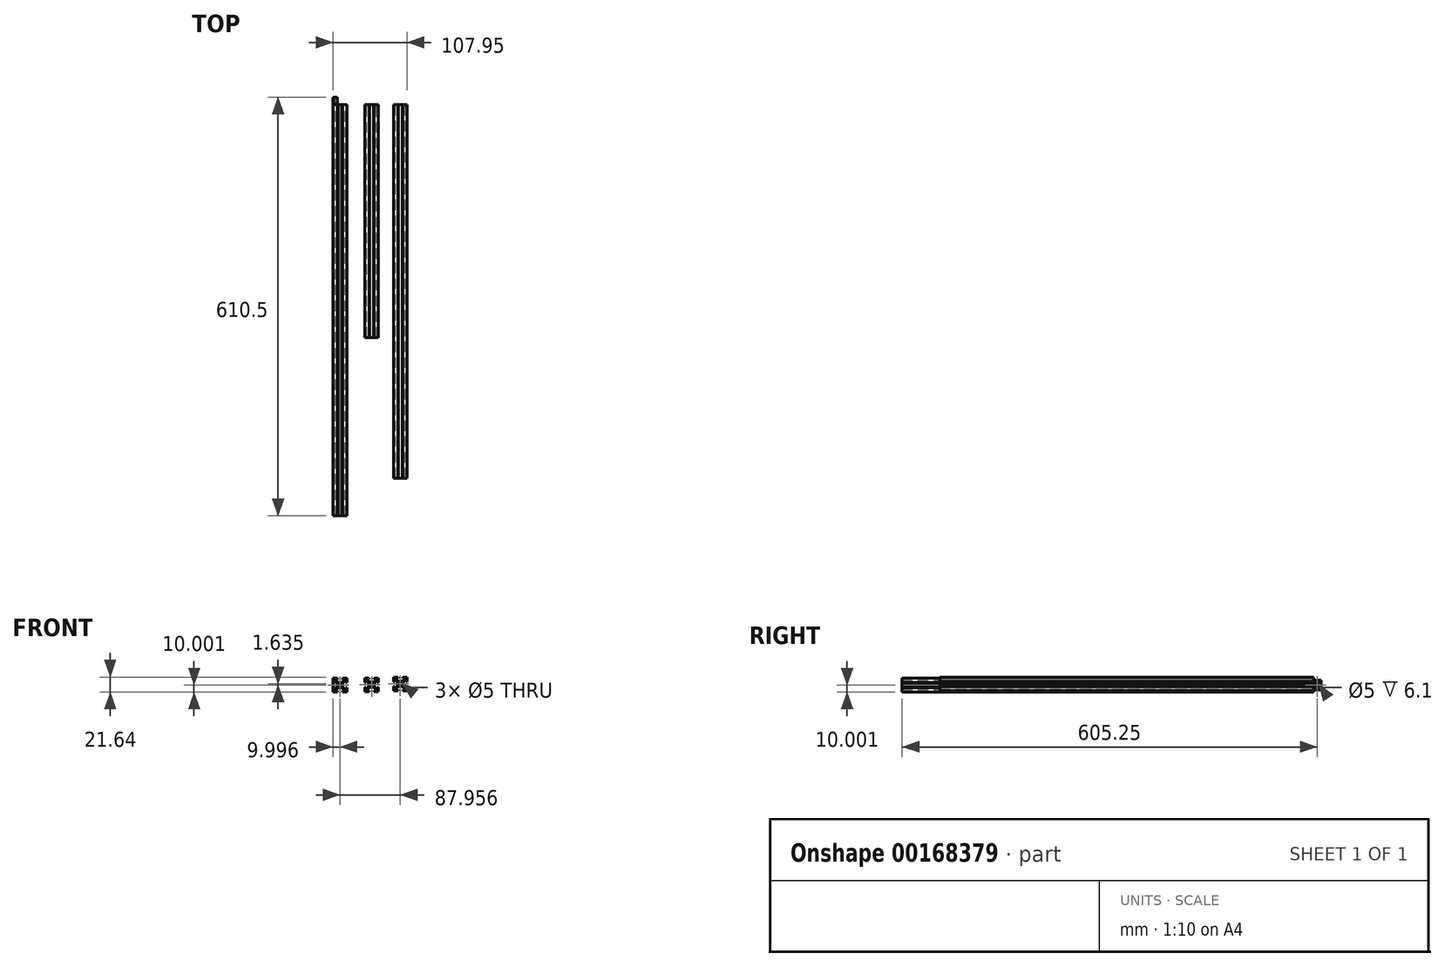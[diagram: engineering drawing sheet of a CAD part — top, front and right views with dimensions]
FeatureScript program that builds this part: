
annotation { "Feature Type Name" : "Feature", "Feature Type Description" : "" }
export const myFeature = defineFeature(function(context is Context, id is Id, definition is map)
    precondition{}
    {
        {
            var Q0;
            Q0=qCreatedBy(makeId("Front.planeOp"),FACE);
            var sketch = newSketch(context, id + "F0", { "sketchPlane" : qUnion([Q0])});
            skLineSegment(sketch, "E0", {"start": v(-6.67, 58.37) * mm, "end": v(-13.07, 58.37) * mm});
            skLineSegment(sketch, "E1", {"start": v(-13.07, 58.37) * mm, "end": v(-13.07, 51.97) * mm});
            skLineSegment(sketch, "E2", {"start": v(-13.07, 51.97) * mm, "end": v(-11.54, 51.97) * mm});
            skLineSegment(sketch, "E3", {"start": v(-11.54, 51.97) * mm, "end": v(-11.54, 55.42) * mm});
            skLineSegment(sketch, "E4", {"start": v(-11.54, 55.42) * mm, "end": v(-6.97, 50.81) * mm});
            skLineSegment(sketch, "E5", {"start": v(-6.97, 50.81) * mm, "end": v(-6.97, 45.93) * mm});
            skLineSegment(sketch, "E6", {"start": v(-6.97, 45.93) * mm, "end": v(-11.54, 41.32) * mm});
            skLineSegment(sketch, "E7", {"start": v(-11.54, 41.32) * mm, "end": v(-11.54, 44.77) * mm});
            skLineSegment(sketch, "E8", {"start": v(-11.54, 44.77) * mm, "end": v(-13.07, 44.77) * mm});
            skLineSegment(sketch, "E9", {"start": v(-13.07, 44.77) * mm, "end": v(-13.07, 38.37) * mm});
            skLineSegment(sketch, "E10", {"start": v(-13.07, 38.37) * mm, "end": v(-6.67, 38.37) * mm});
            skLineSegment(sketch, "E11", {"start": v(-6.67, 38.37) * mm, "end": v(-6.67, 39.9) * mm});
            skLineSegment(sketch, "E12", {"start": v(-6.67, 39.9) * mm, "end": v(-10.13, 39.9) * mm});
            skLineSegment(sketch, "E13", {"start": v(-10.13, 39.9) * mm, "end": v(-5.57, 44.5) * mm});
            skLineSegment(sketch, "E14", {"start": v(-5.57, 44.5) * mm, "end": v(-0.58, 44.5) * mm});
            skLineSegment(sketch, "E15", {"start": v(-0.58, 44.5) * mm, "end": v(3.98, 39.9) * mm});
            skLineSegment(sketch, "E16", {"start": v(3.98, 39.9) * mm, "end": v(0.53, 39.9) * mm});
            skLineSegment(sketch, "E17", {"start": v(0.53, 39.9) * mm, "end": v(0.53, 38.37) * mm});
            skLineSegment(sketch, "E18", {"start": v(0.53, 38.37) * mm, "end": v(6.93, 38.37) * mm});
            skLineSegment(sketch, "E19", {"start": v(6.93, 38.37) * mm, "end": v(6.93, 44.77) * mm});
            skLineSegment(sketch, "E20", {"start": v(6.93, 44.77) * mm, "end": v(5.4, 44.77) * mm});
            skLineSegment(sketch, "E21", {"start": v(5.4, 44.77) * mm, "end": v(5.4, 41.32) * mm});
            skLineSegment(sketch, "E22", {"start": v(5.4, 41.32) * mm, "end": v(0.83, 45.93) * mm});
            skLineSegment(sketch, "E23", {"start": v(0.83, 45.93) * mm, "end": v(0.83, 50.81) * mm});
            skLineSegment(sketch, "E24", {"start": v(0.83, 50.81) * mm, "end": v(5.4, 55.42) * mm});
            skLineSegment(sketch, "E25", {"start": v(5.4, 55.42) * mm, "end": v(5.4, 51.97) * mm});
            skLineSegment(sketch, "E26", {"start": v(5.4, 51.97) * mm, "end": v(6.93, 51.97) * mm});
            skLineSegment(sketch, "E27", {"start": v(6.93, 51.97) * mm, "end": v(6.93, 58.37) * mm});
            skLineSegment(sketch, "E28", {"start": v(6.93, 58.37) * mm, "end": v(0.53, 58.37) * mm});
            skLineSegment(sketch, "E29", {"start": v(0.53, 58.37) * mm, "end": v(0.53, 56.84) * mm});
            skLineSegment(sketch, "E30", {"start": v(0.53, 56.84) * mm, "end": v(3.98, 56.84) * mm});
            skLineSegment(sketch, "E31", {"start": v(3.98, 56.84) * mm, "end": v(-0.58, 52.24) * mm});
            skLineSegment(sketch, "E32", {"start": v(-0.58, 52.24) * mm, "end": v(-5.57, 52.24) * mm});
            skLineSegment(sketch, "E33", {"start": v(-5.57, 52.24) * mm, "end": v(-10.13, 56.84) * mm});
            skLineSegment(sketch, "E34", {"start": v(-10.13, 56.84) * mm, "end": v(-6.67, 56.84) * mm});
            skLineSegment(sketch, "E35", {"start": v(-6.67, 56.84) * mm, "end": v(-6.67, 58.37) * mm});
            skCircle(sketch, "E36", {"center": v(-3.07, 48.37) * mm, "radius": 2.5 * mm});
            skCircle(sketch, "E37", {"center": v(-3.07, 48.37) * mm, "radius": 4.6 * mm, "construction": true});
            skCircle(sketch, "E38", {"center": v(-3.07, 48.37) * mm, "radius": 9.2 * mm, "construction": true});
            skCircle(sketch, "E39", {"center": v(-3.07, 48.37) * mm, "radius": 14.14 * mm, "construction": true});
            skLineSegment(sketch, "E40", {"start": v(39.48, 58.74) * mm, "end": v(33.08, 58.74) * mm});
            skLineSegment(sketch, "E41", {"start": v(33.08, 58.74) * mm, "end": v(33.08, 52.34) * mm});
            skLineSegment(sketch, "E42", {"start": v(33.08, 52.34) * mm, "end": v(34.6, 52.34) * mm});
            skLineSegment(sketch, "E43", {"start": v(34.6, 52.34) * mm, "end": v(34.6, 55.8) * mm});
            skLineSegment(sketch, "E44", {"start": v(34.6, 55.8) * mm, "end": v(39.05, 50.97) * mm});
            skLineSegment(sketch, "E45", {"start": v(39.05, 50.97) * mm, "end": v(39.05, 46.52) * mm});
            skLineSegment(sketch, "E46", {"start": v(39.05, 46.52) * mm, "end": v(34.6, 41.68) * mm});
            skLineSegment(sketch, "E47", {"start": v(34.6, 41.68) * mm, "end": v(34.6, 45.14) * mm});
            skLineSegment(sketch, "E48", {"start": v(34.6, 45.14) * mm, "end": v(33.08, 45.14) * mm});
            skLineSegment(sketch, "E49", {"start": v(33.08, 45.14) * mm, "end": v(33.08, 38.74) * mm});
            skLineSegment(sketch, "E50", {"start": v(33.08, 38.74) * mm, "end": v(39.48, 38.74) * mm});
            skLineSegment(sketch, "E51", {"start": v(39.48, 38.74) * mm, "end": v(39.48, 40.27) * mm});
            skLineSegment(sketch, "E52", {"start": v(39.48, 40.27) * mm, "end": v(36.02, 40.27) * mm});
            skLineSegment(sketch, "E53", {"start": v(36.02, 40.27) * mm, "end": v(40.38, 45.01) * mm});
            skLineSegment(sketch, "E54", {"start": v(40.38, 45.01) * mm, "end": v(45.77, 45.01) * mm});
            skLineSegment(sketch, "E55", {"start": v(45.77, 45.01) * mm, "end": v(50.14, 40.27) * mm});
            skLineSegment(sketch, "E56", {"start": v(50.14, 40.27) * mm, "end": v(46.68, 40.27) * mm});
            skLineSegment(sketch, "E57", {"start": v(46.68, 40.27) * mm, "end": v(46.68, 38.74) * mm});
            skLineSegment(sketch, "E58", {"start": v(46.68, 38.74) * mm, "end": v(53.08, 38.74) * mm});
            skLineSegment(sketch, "E59", {"start": v(53.08, 38.74) * mm, "end": v(53.08, 45.14) * mm});
            skLineSegment(sketch, "E60", {"start": v(53.08, 45.14) * mm, "end": v(51.56, 45.14) * mm});
            skLineSegment(sketch, "E61", {"start": v(51.56, 45.14) * mm, "end": v(51.56, 41.68) * mm});
            skLineSegment(sketch, "E62", {"start": v(51.56, 41.68) * mm, "end": v(47.1, 46.52) * mm});
            skLineSegment(sketch, "E63", {"start": v(47.1, 46.52) * mm, "end": v(47.1, 50.97) * mm});
            skLineSegment(sketch, "E64", {"start": v(47.1, 50.97) * mm, "end": v(51.56, 55.8) * mm});
            skLineSegment(sketch, "E65", {"start": v(51.56, 55.8) * mm, "end": v(51.56, 52.34) * mm});
            skLineSegment(sketch, "E66", {"start": v(51.56, 52.34) * mm, "end": v(53.08, 52.34) * mm});
            skLineSegment(sketch, "E67", {"start": v(53.08, 52.34) * mm, "end": v(53.08, 58.74) * mm});
            skLineSegment(sketch, "E68", {"start": v(53.08, 58.74) * mm, "end": v(46.68, 58.74) * mm});
            skLineSegment(sketch, "E69", {"start": v(46.68, 58.74) * mm, "end": v(46.68, 57.22) * mm});
            skLineSegment(sketch, "E70", {"start": v(46.68, 57.22) * mm, "end": v(50.14, 57.22) * mm});
            skLineSegment(sketch, "E71", {"start": v(50.14, 57.22) * mm, "end": v(45.77, 52.48) * mm});
            skLineSegment(sketch, "E72", {"start": v(45.77, 52.48) * mm, "end": v(40.38, 52.48) * mm});
            skLineSegment(sketch, "E73", {"start": v(40.38, 52.48) * mm, "end": v(36.02, 57.22) * mm});
            skLineSegment(sketch, "E74", {"start": v(36.02, 57.22) * mm, "end": v(39.48, 57.22) * mm});
            skLineSegment(sketch, "E75", {"start": v(39.48, 57.22) * mm, "end": v(39.48, 58.74) * mm});
            skCircle(sketch, "E76", {"center": v(43.08, 48.74) * mm, "radius": 2.5 * mm});
            skCircle(sketch, "E77", {"center": v(43.08, 48.74) * mm, "radius": 4.6 * mm, "construction": true});
            skCircle(sketch, "E78", {"center": v(43.08, 48.74) * mm, "radius": 9.2 * mm, "construction": true});
            skCircle(sketch, "E79", {"center": v(43.08, 48.74) * mm, "radius": 14.14 * mm, "construction": true});
            skLineSegment(sketch, "E80.bottom", {"start": v(-13.07, 58.37) * mm, "end": v(6.93, 58.37) * mm, "construction": true});
            skLineSegment(sketch, "E80.top", {"start": v(-13.07, 38.37) * mm, "end": v(6.93, 38.37) * mm, "construction": true});
            skLineSegment(sketch, "E80.left", {"start": v(-13.07, 58.37) * mm, "end": v(-13.07, 38.37) * mm, "construction": true});
            skLineSegment(sketch, "E80.right", {"start": v(6.93, 58.37) * mm, "end": v(6.93, 38.37) * mm, "construction": true});
            skLineSegment(sketch, "E81", {"start": v(81.28, 60) * mm, "end": v(74.88, 60) * mm});
            skLineSegment(sketch, "E82", {"start": v(74.88, 60) * mm, "end": v(74.88, 53.6) * mm});
            skLineSegment(sketch, "E83", {"start": v(74.88, 53.6) * mm, "end": v(76.4, 53.6) * mm});
            skLineSegment(sketch, "E84", {"start": v(76.4, 53.6) * mm, "end": v(76.4, 57.07) * mm});
            skLineSegment(sketch, "E85", {"start": v(76.4, 57.07) * mm, "end": v(80.85, 52.22) * mm});
            skLineSegment(sketch, "E86", {"start": v(80.85, 52.22) * mm, "end": v(80.85, 47.79) * mm});
            skLineSegment(sketch, "E87", {"start": v(80.85, 47.79) * mm, "end": v(76.4, 42.94) * mm});
            skLineSegment(sketch, "E88", {"start": v(76.4, 42.94) * mm, "end": v(76.4, 46.4) * mm});
            skLineSegment(sketch, "E89", {"start": v(76.4, 46.4) * mm, "end": v(74.88, 46.4) * mm});
            skLineSegment(sketch, "E90", {"start": v(74.88, 46.4) * mm, "end": v(74.88, 40) * mm});
            skLineSegment(sketch, "E91", {"start": v(74.88, 40) * mm, "end": v(81.28, 40) * mm});
            skLineSegment(sketch, "E92", {"start": v(81.28, 40) * mm, "end": v(81.28, 41.53) * mm});
            skLineSegment(sketch, "E93", {"start": v(81.28, 41.53) * mm, "end": v(77.82, 41.53) * mm});
            skLineSegment(sketch, "E94", {"start": v(77.82, 41.53) * mm, "end": v(82.18, 46.28) * mm});
            skLineSegment(sketch, "E95", {"start": v(82.18, 46.28) * mm, "end": v(87.59, 46.28) * mm});
            skLineSegment(sketch, "E96", {"start": v(87.59, 46.28) * mm, "end": v(91.95, 41.53) * mm});
            skLineSegment(sketch, "E97", {"start": v(91.95, 41.53) * mm, "end": v(88.48, 41.53) * mm});
            skLineSegment(sketch, "E98", {"start": v(88.48, 41.53) * mm, "end": v(88.48, 40) * mm});
            skLineSegment(sketch, "E99", {"start": v(88.48, 40) * mm, "end": v(94.88, 40) * mm});
            skLineSegment(sketch, "E100", {"start": v(94.88, 40) * mm, "end": v(94.88, 46.4) * mm});
            skLineSegment(sketch, "E101", {"start": v(94.88, 46.4) * mm, "end": v(93.36, 46.4) * mm});
            skLineSegment(sketch, "E102", {"start": v(93.36, 46.4) * mm, "end": v(93.36, 42.94) * mm});
            skLineSegment(sketch, "E103", {"start": v(93.36, 42.94) * mm, "end": v(88.92, 47.79) * mm});
            skLineSegment(sketch, "E104", {"start": v(88.92, 47.79) * mm, "end": v(88.92, 52.22) * mm});
            skLineSegment(sketch, "E105", {"start": v(88.92, 52.22) * mm, "end": v(93.36, 57.07) * mm});
            skLineSegment(sketch, "E106", {"start": v(93.36, 57.07) * mm, "end": v(93.36, 53.6) * mm});
            skLineSegment(sketch, "E107", {"start": v(93.36, 53.6) * mm, "end": v(94.88, 53.6) * mm});
            skLineSegment(sketch, "E108", {"start": v(94.88, 53.6) * mm, "end": v(94.88, 60) * mm});
            skLineSegment(sketch, "E109", {"start": v(94.88, 60) * mm, "end": v(88.48, 60) * mm});
            skLineSegment(sketch, "E110", {"start": v(88.48, 60) * mm, "end": v(88.48, 58.48) * mm});
            skLineSegment(sketch, "E111", {"start": v(88.48, 58.48) * mm, "end": v(91.95, 58.48) * mm});
            skLineSegment(sketch, "E112", {"start": v(91.95, 58.48) * mm, "end": v(87.59, 53.73) * mm});
            skLineSegment(sketch, "E113", {"start": v(87.59, 53.73) * mm, "end": v(82.18, 53.73) * mm});
            skLineSegment(sketch, "E114", {"start": v(82.18, 53.73) * mm, "end": v(77.82, 58.48) * mm});
            skLineSegment(sketch, "E115", {"start": v(77.82, 58.48) * mm, "end": v(81.28, 58.48) * mm});
            skLineSegment(sketch, "E116", {"start": v(81.28, 58.48) * mm, "end": v(81.28, 60) * mm});
            skCircle(sketch, "E117", {"center": v(84.88, 50) * mm, "radius": 2.5 * mm});
            skCircle(sketch, "E118", {"center": v(84.88, 50) * mm, "radius": 4.6 * mm, "construction": true});
            skCircle(sketch, "E119", {"center": v(84.88, 50) * mm, "radius": 9.2 * mm, "construction": true});
            skCircle(sketch, "E120", {"center": v(84.88, 50) * mm, "radius": 14.14 * mm, "construction": true});
            skLineSegment(sketch, "E121", {"start": v(-13.07, 51.97) * mm, "end": v(-13.07, 44.77) * mm});
            skSolve(sketch);
        }
        {
            var Q0;
            Q0=makeQuery(id+"F0.imprint","IMPRINT",FACE,{"disambiguationData":[TD([[makeQuery(id+"F0.imprint","IMPRINT",EDGE,{"derivedFrom":sQuery(id+"F0.wireOp",EDGE,"E0")}),1.0]])]});
            extrude(context, id + "F1", {"entities" : qUnion([Q0]), "depth" : 600 * mm});
        }
        {
            var Q0;
            Q0=makeQuery(id+"F0.imprint","IMPRINT",FACE,{"disambiguationData":[TD([[makeQuery(id+"F0.imprint","IMPRINT",EDGE,{"derivedFrom":sQuery(id+"F0.wireOp",EDGE,"E40")}),1.0]])]});
            extrude(context, id + "F2", {"entities" : qUnion([Q0]), "depth" : 340 * mm});
        }
        {
            var Q0;
            Q0=makeQuery(id+"F0.imprint","IMPRINT",FACE,{"disambiguationData":[TD([[makeQuery(id+"F0.imprint","IMPRINT",EDGE,{"derivedFrom":sQuery(id+"F0.wireOp",EDGE,"E81")}),1.0]])]});
            extrude(context, id + "F3", {"entities" : qUnion([Q0]), "depth" : 545 * mm});
        }
        {
            var Q0;
            Q0=makeQuery(id+"F0.imprint","IMPRINT",FACE,{"disambiguationData":[TD([[makeQuery(id+"F0.imprint","IMPRINT",EDGE,{"derivedFrom":sQuery(id+"F0.wireOp",EDGE,"E2")}),-1.0]])]});
            extrude(context, id + "F4", {"entities" : qUnion([Q0]), "oppositeDirection" : true, "depth" : 10.5 * mm});
        }
        {
            var Q0;
            Q0=makeQuery(id+"F4.opExtrude","SWEPT_FACE",FACE,{"disambiguationData":[OSD([sQuery(id+"F0.wireOp",EDGE,"E121")])]});
            var sketch = newSketch(context, id + "F5", { "sketchPlane" : qUnion([Q0])});
            skLineSegment(sketch, "E122", {"start": v(-10.5, 48.37) * mm, "end": v(0, 48.37) * mm, "construction": true});
            skCircle(sketch, "E123", {"center": v(-5.25, 48.37) * mm, "radius": 2.5 * mm});
            skSolve(sketch);
        }
        {
            var Q0;
            Q0=makeQuery(id+"F5.imprint","IMPRINT",FACE,{"disambiguationData":[TD([[makeQuery(id+"F5.imprint","IMPRINT",EDGE,{"derivedFrom":sQuery(id+"F5.wireOp",EDGE,"E123")}),1.0]])]});
            extrude(context, id + "F6", {"entities" : qUnion([Q0]), "operationType" : NewBodyOperationType.REMOVE, "oppositeDirection" : true, "depth" : 25 * mm});
        }
    });
